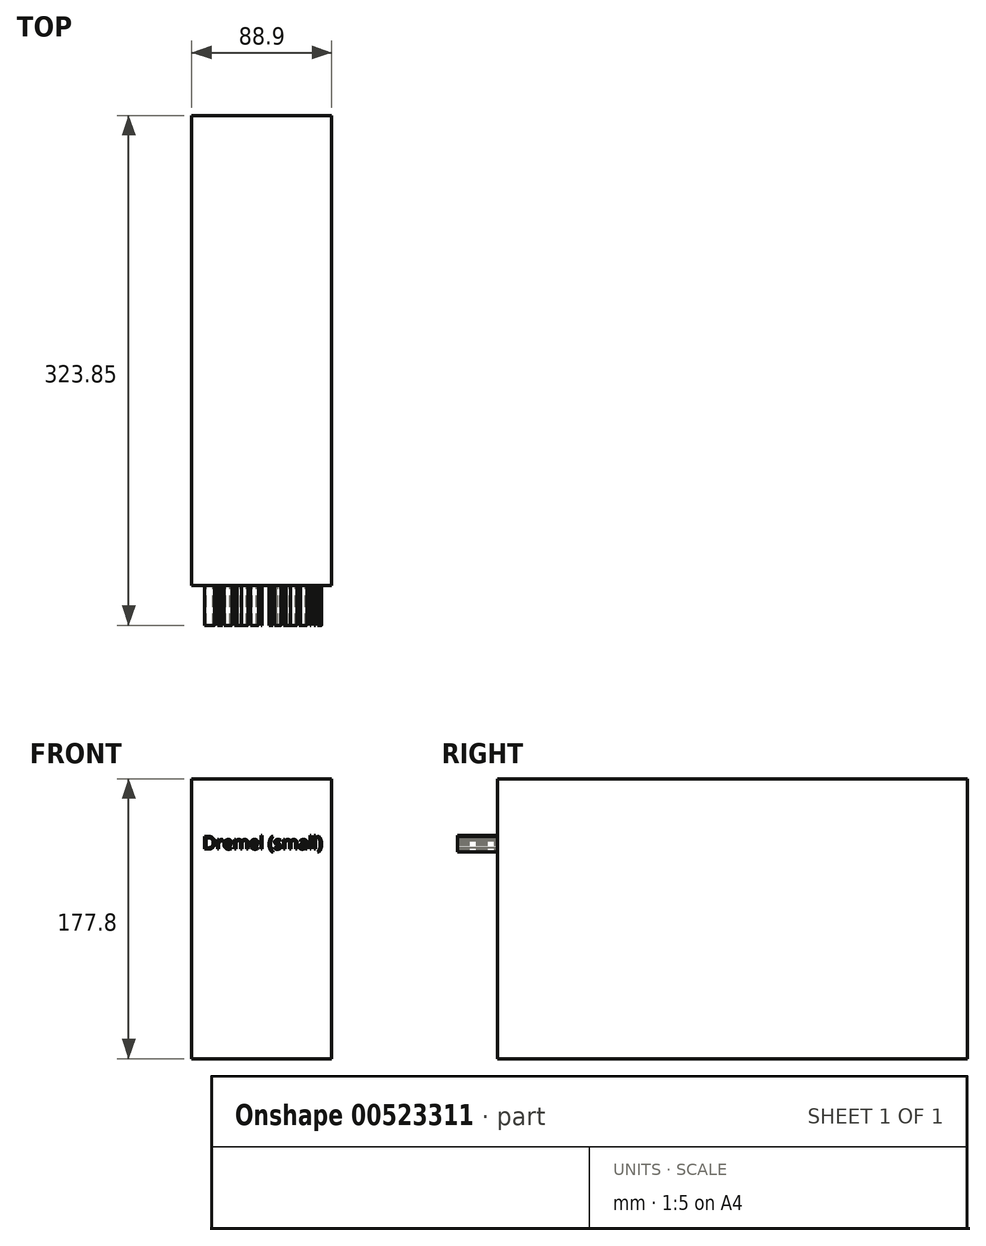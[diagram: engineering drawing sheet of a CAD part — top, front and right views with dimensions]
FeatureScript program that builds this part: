
annotation { "Feature Type Name" : "Feature", "Feature Type Description" : "" }
export const myFeature = defineFeature(function(context is Context, id is Id, definition is map)
    precondition{}
    {
        {
            var Q0;
            Q0=qCreatedBy(makeId("Front.planeOp"),FACE);
            var sketch = newSketch(context, id + "F0", { "sketchPlane" : qUnion([Q0])});
            skLineSegment(sketch, "E0.bottom", {"start": v(44.45, 88.9) * mm, "end": v(-44.45, 88.9) * mm});
            skLineSegment(sketch, "E0.top", {"start": v(44.45, -88.9) * mm, "end": v(-44.45, -88.9) * mm});
            skLineSegment(sketch, "E0.left", {"start": v(44.45, 88.9) * mm, "end": v(44.45, -88.9) * mm});
            skLineSegment(sketch, "E0.right", {"start": v(-44.45, 88.9) * mm, "end": v(-44.45, -88.9) * mm});
            skPoint(sketch, "E0.middle", {"position": v(0, 0) * mm});
            skSolve(sketch);
        }
        {
            var Q0;
            Q0=makeQuery(id+"F0.imprint","IMPRINT",FACE,{"disambiguationData":[TD([[makeQuery(id+"F0.imprint","IMPRINT",EDGE,{"derivedFrom":sQuery(id+"F0.wireOp",EDGE,"E0.bottom")}),1.0]])]});
            extrude(context, id + "F1", {"entities" : qUnion([Q0]), "depth" : 298.45 * mm, "offsetDistance" : 25.4 * mm});
        }
        {
            var Q0;
            Q0=makeQuery(id+"F1.opExtrude","CAP_FACE",FACE,{"disambiguationData":[OSD([sQuery(id+"F0.wireOp",EDGE,"E0.bottom"),sQuery(id+"F0.wireOp",EDGE,"E0.top"),sQuery(id+"F0.wireOp",EDGE,"E0.left"),sQuery(id+"F0.wireOp",EDGE,"E0.right")])],"isStart":false});
            var sketch = newSketch(context, id + "F2", { "sketchPlane" : qUnion([Q0])});
            skText(sketch, "E1", { "text": "Dremel (small)", "fontName": "OpenSans-Regular.ttf"});
            const initialGuessF2  = {"E1": [-0.03738, 0.04423, 1, 0, 0.00808]};
            skSetInitialGuess(sketch, initialGuessF2);
            skSolve(sketch);
        }
        {
            var Q0;
            Q0 = qSketchRegion(id + "F2", true);
            extrude(context, id + "F3", {"entities" : qUnion([Q0]), "operationType" : NewBodyOperationType.ADD, "depth" : 25.4 * mm, "offsetDistance" : 25.4 * mm});
        }
    });
